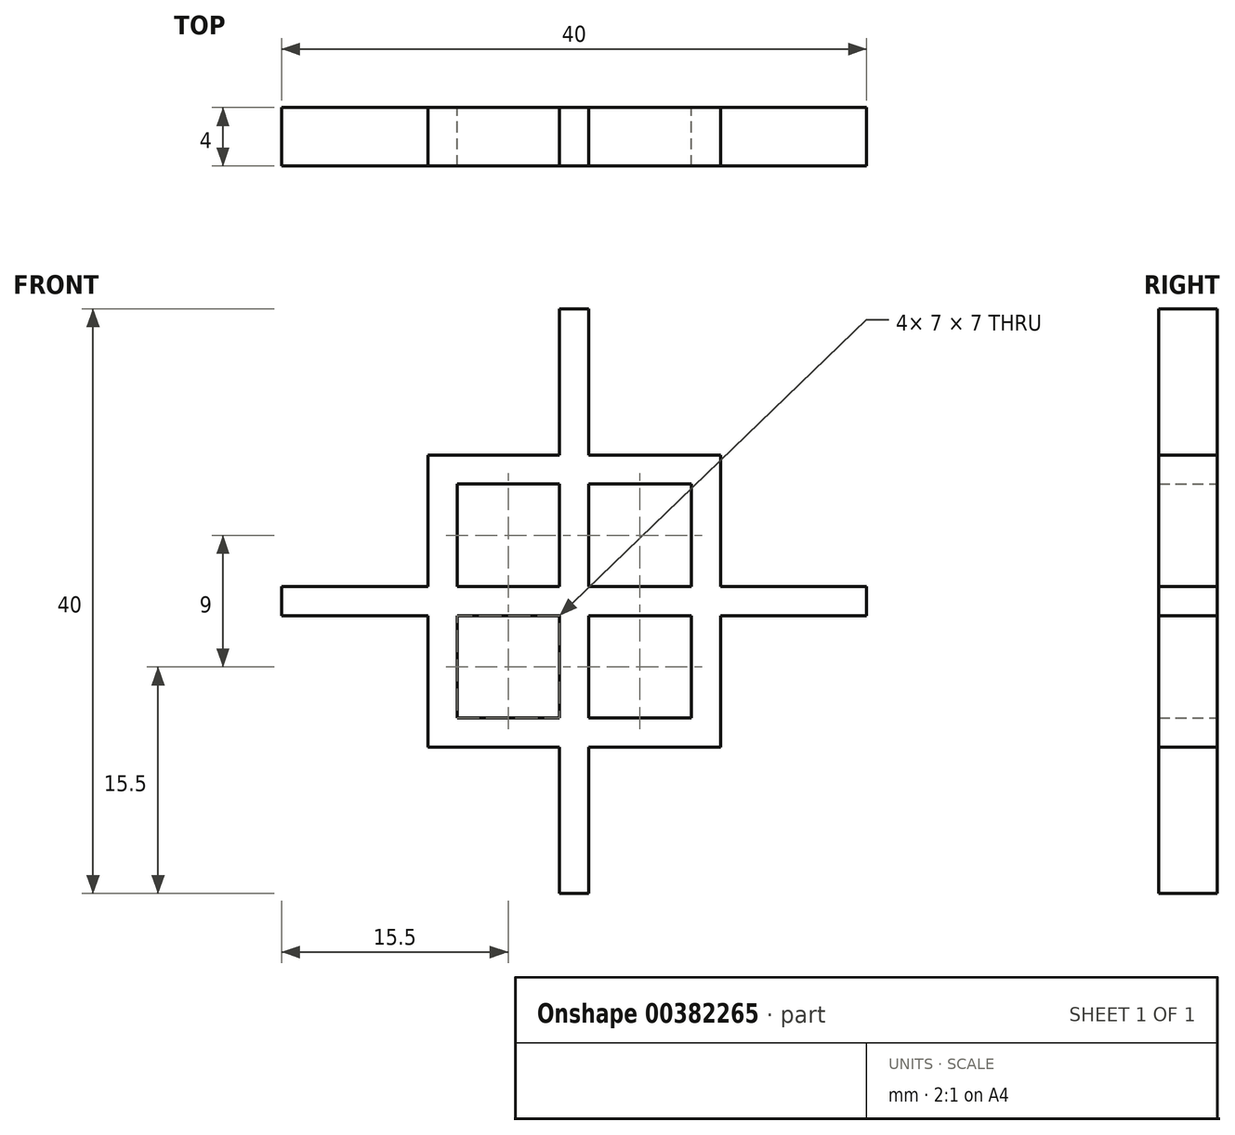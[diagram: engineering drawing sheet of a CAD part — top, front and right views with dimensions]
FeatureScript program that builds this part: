
annotation { "Feature Type Name" : "Feature", "Feature Type Description" : "" }
export const myFeature = defineFeature(function(context is Context, id is Id, definition is map)
    precondition{}
    {
        {
            var Q0;
            Q0=qCreatedBy(makeId("Front.planeOp"),FACE);
            var sketch = newSketch(context, id + "F0", { "sketchPlane" : qUnion([Q0])});
            skPoint(sketch, "E0", {"position": v(20, 0) * mm});
            skPoint(sketch, "E1", {"position": v(0, 20) * mm});
            skLineSegment(sketch, "E2", {"start": v(20, 0) * mm, "end": v(20, 20) * mm});
            skLineSegment(sketch, "E3", {"start": v(20, 20) * mm, "end": v(0, 20) * mm});
            skLineSegment(sketch, "E4", {"start": v(20, 0) * mm, "end": v(20, -20) * mm});
            skLineSegment(sketch, "E5", {"start": v(20, -20) * mm, "end": v(0, -20) * mm});
            skLineSegment(sketch, "E6", {"start": v(0, -20) * mm, "end": v(0, 20) * mm});
            skLineSegment(sketch, "E7.MirrorCS", {"start": v(-20, 20) * mm, "end": v(0, 20) * mm});
            skLineSegment(sketch, "E8.MirrorCS", {"start": v(-20, 0) * mm, "end": v(-20, -20) * mm});
            skLineSegment(sketch, "E9.MirrorCS", {"start": v(-20, -20) * mm, "end": v(0, -20) * mm});
            skLineSegment(sketch, "E10.MirrorCS", {"start": v(-20, 0) * mm, "end": v(-20, 20) * mm});
            skPoint(sketch, "E11", {"position": v(20, -1) * mm});
            skPoint(sketch, "E12", {"position": v(-1, 20) * mm});
            skPoint(sketch, "E13", {"position": v(-20, -1) * mm});
            skPoint(sketch, "E14", {"position": v(1, -20) * mm});
            skPoint(sketch, "E15", {"position": v(8, 19.86) * mm});
            skPoint(sketch, "E16", {"position": v(-8, 20) * mm});
            skPoint(sketch, "E17", {"position": v(20, 8) * mm});
            skPoint(sketch, "E18", {"position": v(20, -8) * mm});
            skLineSegment(sketch, "E19", {"start": v(-20, 0) * mm, "end": v(20, 0) * mm});
            skPoint(sketch, "E20.MirrorP", {"position": v(1, 20) * mm});
            skPoint(sketch, "E21.MirrorP", {"position": v(-20, 8) * mm});
            skPoint(sketch, "E22.MirrorP", {"position": v(-20, -8) * mm});
            skPoint(sketch, "E23.MirrorP", {"position": v(8, -19.86) * mm});
            skPoint(sketch, "E24.MirrorP", {"position": v(-8, -20) * mm});
            skPoint(sketch, "E25.MirrorP", {"position": v(20, 1) * mm});
            skLineSegment(sketch, "E26.bottom", {"start": v(-20, -1) * mm, "end": v(20, -1) * mm});
            skLineSegment(sketch, "E26.top", {"start": v(-20, 1) * mm, "end": v(20, 1) * mm});
            skLineSegment(sketch, "E26.left", {"start": v(-20, -1) * mm, "end": v(-20, 1) * mm});
            skLineSegment(sketch, "E26.right", {"start": v(20, -1) * mm, "end": v(20, 1) * mm});
            skLineSegment(sketch, "E27.bottom", {"start": v(-1, 20) * mm, "end": v(1, 20) * mm});
            skLineSegment(sketch, "E27.top", {"start": v(-1, -20) * mm, "end": v(1, -20) * mm});
            skLineSegment(sketch, "E27.left", {"start": v(-1, 20) * mm, "end": v(-1, -20) * mm});
            skLineSegment(sketch, "E27.right", {"start": v(1, 20) * mm, "end": v(1, -20) * mm});
            skLineSegment(sketch, "E28.bottom", {"start": v(8, 19.86) * mm, "end": v(10, 19.86) * mm});
            skLineSegment(sketch, "E28.top", {"start": v(8, -20) * mm, "end": v(10, -20) * mm});
            skLineSegment(sketch, "E28.left", {"start": v(8, 19.86) * mm, "end": v(8, -20) * mm});
            skLineSegment(sketch, "E28.right", {"start": v(10, 19.86) * mm, "end": v(10, -20) * mm});
            skLineSegment(sketch, "E29.bottom", {"start": v(-8, 20) * mm, "end": v(-10, 20) * mm});
            skLineSegment(sketch, "E29.top", {"start": v(-8, -20) * mm, "end": v(-10, -20) * mm});
            skLineSegment(sketch, "E29.left", {"start": v(-8, 20) * mm, "end": v(-8, -20) * mm});
            skLineSegment(sketch, "E29.right", {"start": v(-10, 20) * mm, "end": v(-10, -20) * mm});
            skLineSegment(sketch, "E30.bottom", {"start": v(-20, 8) * mm, "end": v(20, 8) * mm});
            skLineSegment(sketch, "E30.top", {"start": v(-20, 10) * mm, "end": v(20, 10) * mm});
            skLineSegment(sketch, "E30.left", {"start": v(-20, 8) * mm, "end": v(-20, 10) * mm});
            skLineSegment(sketch, "E30.right", {"start": v(20, 8) * mm, "end": v(20, 10) * mm});
            skLineSegment(sketch, "E31.bottom", {"start": v(-20, -8) * mm, "end": v(20, -8) * mm});
            skLineSegment(sketch, "E31.top", {"start": v(-20, -10) * mm, "end": v(20, -10) * mm});
            skLineSegment(sketch, "E31.left", {"start": v(-20, -8) * mm, "end": v(-20, -10) * mm});
            skLineSegment(sketch, "E31.right", {"start": v(20, -8) * mm, "end": v(20, -10) * mm});
            skSolve(sketch);
        }
        {
            var Q0;
            {var subQ0=sQuery(id+"F0.wireOp",EDGE,"E27.bottom");var subQ1=sQuery(id+"F0.wireOp",EDGE,"E6");var subQ2=makeQuery(id+"F0.imprint","INTERSECT",VERTEX,{"derivedFrom":[subQ1,subQ0]});Q0=makeQuery(id+"F0.imprint","IMPRINT",FACE,{"disambiguationData":[TD([[makeQuery(id+"F0.imprint","IMPRINT",EDGE,{"disambiguationData":[TD([[subQ2,1.0]])],"derivedFrom":subQ1}),1.0]])]});}
            var Q1;
            {var subQ0=sQuery(id+"F0.wireOp",EDGE,"E27.bottom");var subQ1=sQuery(id+"F0.wireOp",EDGE,"E6");var subQ2=makeQuery(id+"F0.imprint","INTERSECT",VERTEX,{"derivedFrom":[subQ1,subQ0]});Q1=makeQuery(id+"F0.imprint","IMPRINT",FACE,{"disambiguationData":[TD([[makeQuery(id+"F0.imprint","IMPRINT",EDGE,{"disambiguationData":[TD([[subQ2,1.0]])],"derivedFrom":subQ1}),-1.0]])]});}
            var Q2;
            {var subQ0=sQuery(id+"F0.wireOp",EDGE,"E30.bottom");var subQ1=sQuery(id+"F0.wireOp",EDGE,"E6");var subQ2=makeQuery(id+"F0.imprint","INTERSECT",VERTEX,{"derivedFrom":[subQ1,subQ0]});Q2=makeQuery(id+"F0.imprint","IMPRINT",FACE,{"disambiguationData":[TD([[makeQuery(id+"F0.imprint","IMPRINT",EDGE,{"disambiguationData":[TD([[subQ2,-1.0]])],"derivedFrom":subQ1}),-1.0]])]});}
            var Q3;
            {var subQ0=sQuery(id+"F0.wireOp",EDGE,"E30.bottom");var subQ1=sQuery(id+"F0.wireOp",EDGE,"E6");var subQ2=makeQuery(id+"F0.imprint","INTERSECT",VERTEX,{"derivedFrom":[subQ1,subQ0]});Q3=makeQuery(id+"F0.imprint","IMPRINT",FACE,{"disambiguationData":[TD([[makeQuery(id+"F0.imprint","IMPRINT",EDGE,{"disambiguationData":[TD([[subQ2,-1.0]])],"derivedFrom":subQ1}),1.0]])]});}
            var Q4;
            {var subQ0=sQuery(id+"F0.wireOp",EDGE,"E30.top");var subQ1=sQuery(id+"F0.wireOp",EDGE,"E27.right");var subQ2=makeQuery(id+"F0.imprint","INTERSECT",VERTEX,{"derivedFrom":[subQ1,subQ0]});Q4=makeQuery(id+"F0.imprint","IMPRINT",FACE,{"disambiguationData":[TD([[makeQuery(id+"F0.imprint","IMPRINT",EDGE,{"disambiguationData":[TD([[subQ2,-1.0]])],"derivedFrom":subQ1}),1.0]])]});}
            var Q5;
            {var subQ0=sQuery(id+"F0.wireOp",EDGE,"E30.top");var subQ1=sQuery(id+"F0.wireOp",EDGE,"E27.left");var subQ2=makeQuery(id+"F0.imprint","INTERSECT",VERTEX,{"derivedFrom":[subQ1,subQ0]});Q5=makeQuery(id+"F0.imprint","IMPRINT",FACE,{"disambiguationData":[TD([[makeQuery(id+"F0.imprint","IMPRINT",EDGE,{"disambiguationData":[TD([[subQ2,-1.0]])],"derivedFrom":subQ1}),-1.0]])]});}
            var Q6;
            {var subQ0=sQuery(id+"F0.wireOp",EDGE,"E30.top");var subQ1=sQuery(id+"F0.wireOp",EDGE,"E28.left");var subQ2=makeQuery(id+"F0.imprint","INTERSECT",VERTEX,{"derivedFrom":[subQ1,subQ0]});Q6=makeQuery(id+"F0.imprint","IMPRINT",FACE,{"disambiguationData":[TD([[makeQuery(id+"F0.imprint","IMPRINT",EDGE,{"disambiguationData":[TD([[subQ2,-1.0]])],"derivedFrom":subQ1}),1.0]])]});}
            var Q7;
            {var subQ0=sQuery(id+"F0.wireOp",EDGE,"E28.left");var subQ1=sQuery(id+"F0.wireOp",EDGE,"E26.top");var subQ2=makeQuery(id+"F0.imprint","INTERSECT",VERTEX,{"derivedFrom":[subQ1,subQ0]});Q7=makeQuery(id+"F0.imprint","IMPRINT",FACE,{"disambiguationData":[TD([[makeQuery(id+"F0.imprint","IMPRINT",EDGE,{"disambiguationData":[TD([[subQ2,-1.0]])],"derivedFrom":subQ1}),1.0]])]});}
            var Q8;
            {var subQ0=sQuery(id+"F0.wireOp",EDGE,"E28.left");var subQ1=sQuery(id+"F0.wireOp",EDGE,"E26.bottom");var subQ2=makeQuery(id+"F0.imprint","INTERSECT",VERTEX,{"derivedFrom":[subQ1,subQ0]});Q8=makeQuery(id+"F0.imprint","IMPRINT",FACE,{"disambiguationData":[TD([[makeQuery(id+"F0.imprint","IMPRINT",EDGE,{"disambiguationData":[TD([[subQ2,-1.0]])],"derivedFrom":subQ1}),-1.0]])]});}
            var Q9;
            {var subQ0=sQuery(id+"F0.wireOp",EDGE,"E26.right");var subQ1=sQuery(id+"F0.wireOp",EDGE,"E19");var subQ2=makeQuery(id+"F0.imprint","INTERSECT",VERTEX,{"derivedFrom":[subQ1,subQ0]});Q9=makeQuery(id+"F0.imprint","IMPRINT",FACE,{"disambiguationData":[TD([[makeQuery(id+"F0.imprint","IMPRINT",EDGE,{"disambiguationData":[TD([[subQ2,1.0]])],"derivedFrom":subQ1}),1.0]])]});}
            var Q10;
            {var subQ0=sQuery(id+"F0.wireOp",EDGE,"E26.right");var subQ1=sQuery(id+"F0.wireOp",EDGE,"E19");var subQ2=makeQuery(id+"F0.imprint","INTERSECT",VERTEX,{"derivedFrom":[subQ1,subQ0]});Q10=makeQuery(id+"F0.imprint","IMPRINT",FACE,{"disambiguationData":[TD([[makeQuery(id+"F0.imprint","IMPRINT",EDGE,{"disambiguationData":[TD([[subQ2,1.0]])],"derivedFrom":subQ1}),-1.0]])]});}
            var Q11;
            {var subQ0=sQuery(id+"F0.wireOp",EDGE,"E28.left");var subQ1=sQuery(id+"F0.wireOp",EDGE,"E19");var subQ2=makeQuery(id+"F0.imprint","INTERSECT",VERTEX,{"derivedFrom":[subQ1,subQ0]});Q11=makeQuery(id+"F0.imprint","IMPRINT",FACE,{"disambiguationData":[TD([[makeQuery(id+"F0.imprint","IMPRINT",EDGE,{"disambiguationData":[TD([[subQ2,-1.0]])],"derivedFrom":subQ1}),-1.0]])]});}
            var Q12;
            {var subQ0=sQuery(id+"F0.wireOp",EDGE,"E28.left");var subQ1=sQuery(id+"F0.wireOp",EDGE,"E19");var subQ2=makeQuery(id+"F0.imprint","INTERSECT",VERTEX,{"derivedFrom":[subQ1,subQ0]});Q12=makeQuery(id+"F0.imprint","IMPRINT",FACE,{"disambiguationData":[TD([[makeQuery(id+"F0.imprint","IMPRINT",EDGE,{"disambiguationData":[TD([[subQ2,-1.0]])],"derivedFrom":subQ1}),1.0]])]});}
            var Q13;
            {var subQ0=sQuery(id+"F0.wireOp",EDGE,"E31.bottom");var subQ1=sQuery(id+"F0.wireOp",EDGE,"E28.left");var subQ2=makeQuery(id+"F0.imprint","INTERSECT",VERTEX,{"derivedFrom":[subQ1,subQ0]});Q13=makeQuery(id+"F0.imprint","IMPRINT",FACE,{"disambiguationData":[TD([[makeQuery(id+"F0.imprint","IMPRINT",EDGE,{"disambiguationData":[TD([[subQ2,-1.0]])],"derivedFrom":subQ1}),1.0]])]});}
            var Q14;
            {var subQ0=sQuery(id+"F0.wireOp",EDGE,"E31.bottom");var subQ1=sQuery(id+"F0.wireOp",EDGE,"E27.right");var subQ2=makeQuery(id+"F0.imprint","INTERSECT",VERTEX,{"derivedFrom":[subQ1,subQ0]});Q14=makeQuery(id+"F0.imprint","IMPRINT",FACE,{"disambiguationData":[TD([[makeQuery(id+"F0.imprint","IMPRINT",EDGE,{"disambiguationData":[TD([[subQ2,-1.0]])],"derivedFrom":subQ1}),1.0]])]});}
            var Q15;
            {var subQ0=sQuery(id+"F0.wireOp",EDGE,"E31.top");var subQ1=sQuery(id+"F0.wireOp",EDGE,"E6");var subQ2=makeQuery(id+"F0.imprint","INTERSECT",VERTEX,{"derivedFrom":[subQ1,subQ0]});Q15=makeQuery(id+"F0.imprint","IMPRINT",FACE,{"disambiguationData":[TD([[makeQuery(id+"F0.imprint","IMPRINT",EDGE,{"disambiguationData":[TD([[subQ2,-1.0]])],"derivedFrom":subQ1}),-1.0]])]});}
            var Q16;
            {var subQ0=sQuery(id+"F0.wireOp",EDGE,"E31.top");var subQ1=sQuery(id+"F0.wireOp",EDGE,"E6");var subQ2=makeQuery(id+"F0.imprint","INTERSECT",VERTEX,{"derivedFrom":[subQ1,subQ0]});Q16=makeQuery(id+"F0.imprint","IMPRINT",FACE,{"disambiguationData":[TD([[makeQuery(id+"F0.imprint","IMPRINT",EDGE,{"disambiguationData":[TD([[subQ2,-1.0]])],"derivedFrom":subQ1}),1.0]])]});}
            var Q17;
            {var subQ0=sQuery(id+"F0.wireOp",EDGE,"E27.top");var subQ1=sQuery(id+"F0.wireOp",EDGE,"E6");var subQ2=makeQuery(id+"F0.imprint","INTERSECT",VERTEX,{"derivedFrom":[subQ1,subQ0]});Q17=makeQuery(id+"F0.imprint","IMPRINT",FACE,{"disambiguationData":[TD([[makeQuery(id+"F0.imprint","IMPRINT",EDGE,{"disambiguationData":[TD([[subQ2,-1.0]])],"derivedFrom":subQ1}),-1.0]])]});}
            var Q18;
            {var subQ0=sQuery(id+"F0.wireOp",EDGE,"E27.top");var subQ1=sQuery(id+"F0.wireOp",EDGE,"E6");var subQ2=makeQuery(id+"F0.imprint","INTERSECT",VERTEX,{"derivedFrom":[subQ1,subQ0]});Q18=makeQuery(id+"F0.imprint","IMPRINT",FACE,{"disambiguationData":[TD([[makeQuery(id+"F0.imprint","IMPRINT",EDGE,{"disambiguationData":[TD([[subQ2,-1.0]])],"derivedFrom":subQ1}),1.0]])]});}
            var Q19;
            {var subQ0=sQuery(id+"F0.wireOp",EDGE,"E31.bottom");var subQ1=sQuery(id+"F0.wireOp",EDGE,"E27.left");var subQ2=makeQuery(id+"F0.imprint","INTERSECT",VERTEX,{"derivedFrom":[subQ1,subQ0]});Q19=makeQuery(id+"F0.imprint","IMPRINT",FACE,{"disambiguationData":[TD([[makeQuery(id+"F0.imprint","IMPRINT",EDGE,{"disambiguationData":[TD([[subQ2,-1.0]])],"derivedFrom":subQ1}),-1.0]])]});}
            var Q20;
            {var subQ0=sQuery(id+"F0.wireOp",EDGE,"E31.bottom");var subQ1=sQuery(id+"F0.wireOp",EDGE,"E29.left");var subQ2=makeQuery(id+"F0.imprint","INTERSECT",VERTEX,{"derivedFrom":[subQ1,subQ0]});Q20=makeQuery(id+"F0.imprint","IMPRINT",FACE,{"disambiguationData":[TD([[makeQuery(id+"F0.imprint","IMPRINT",EDGE,{"disambiguationData":[TD([[subQ2,-1.0]])],"derivedFrom":subQ1}),-1.0]])]});}
            var Q21;
            {var subQ0=sQuery(id+"F0.wireOp",EDGE,"E29.right");var subQ1=sQuery(id+"F0.wireOp",EDGE,"E26.bottom");var subQ2=makeQuery(id+"F0.imprint","INTERSECT",VERTEX,{"derivedFrom":[subQ1,subQ0]});Q21=makeQuery(id+"F0.imprint","IMPRINT",FACE,{"disambiguationData":[TD([[makeQuery(id+"F0.imprint","IMPRINT",EDGE,{"disambiguationData":[TD([[subQ2,-1.0]])],"derivedFrom":subQ1}),-1.0]])]});}
            var Q22;
            {var subQ0=sQuery(id+"F0.wireOp",EDGE,"E29.right");var subQ1=sQuery(id+"F0.wireOp",EDGE,"E26.top");var subQ2=makeQuery(id+"F0.imprint","INTERSECT",VERTEX,{"derivedFrom":[subQ1,subQ0]});Q22=makeQuery(id+"F0.imprint","IMPRINT",FACE,{"disambiguationData":[TD([[makeQuery(id+"F0.imprint","IMPRINT",EDGE,{"disambiguationData":[TD([[subQ2,-1.0]])],"derivedFrom":subQ1}),1.0]])]});}
            var Q23;
            {var subQ0=sQuery(id+"F0.wireOp",EDGE,"E30.top");var subQ1=sQuery(id+"F0.wireOp",EDGE,"E29.left");var subQ2=makeQuery(id+"F0.imprint","INTERSECT",VERTEX,{"derivedFrom":[subQ1,subQ0]});Q23=makeQuery(id+"F0.imprint","IMPRINT",FACE,{"disambiguationData":[TD([[makeQuery(id+"F0.imprint","IMPRINT",EDGE,{"disambiguationData":[TD([[subQ2,-1.0]])],"derivedFrom":subQ1}),-1.0]])]});}
            var Q24;
            {var subQ0=sQuery(id+"F0.wireOp",EDGE,"E29.right");var subQ1=sQuery(id+"F0.wireOp",EDGE,"E19");var subQ2=makeQuery(id+"F0.imprint","INTERSECT",VERTEX,{"derivedFrom":[subQ1,subQ0]});Q24=makeQuery(id+"F0.imprint","IMPRINT",FACE,{"disambiguationData":[TD([[makeQuery(id+"F0.imprint","IMPRINT",EDGE,{"disambiguationData":[TD([[subQ2,-1.0]])],"derivedFrom":subQ1}),1.0]])]});}
            var Q25;
            {var subQ0=sQuery(id+"F0.wireOp",EDGE,"E29.right");var subQ1=sQuery(id+"F0.wireOp",EDGE,"E19");var subQ2=makeQuery(id+"F0.imprint","INTERSECT",VERTEX,{"derivedFrom":[subQ1,subQ0]});Q25=makeQuery(id+"F0.imprint","IMPRINT",FACE,{"disambiguationData":[TD([[makeQuery(id+"F0.imprint","IMPRINT",EDGE,{"disambiguationData":[TD([[subQ2,-1.0]])],"derivedFrom":subQ1}),-1.0]])]});}
            var Q26;
            {var subQ0=sQuery(id+"F0.wireOp",EDGE,"E26.left");var subQ1=sQuery(id+"F0.wireOp",EDGE,"E19");var subQ2=makeQuery(id+"F0.imprint","INTERSECT",VERTEX,{"derivedFrom":[subQ1,subQ0]});Q26=makeQuery(id+"F0.imprint","IMPRINT",FACE,{"disambiguationData":[TD([[makeQuery(id+"F0.imprint","IMPRINT",EDGE,{"disambiguationData":[TD([[subQ2,-1.0]])],"derivedFrom":subQ1}),1.0]])]});}
            var Q27;
            {var subQ0=sQuery(id+"F0.wireOp",EDGE,"E26.left");var subQ1=sQuery(id+"F0.wireOp",EDGE,"E19");var subQ2=makeQuery(id+"F0.imprint","INTERSECT",VERTEX,{"derivedFrom":[subQ1,subQ0]});Q27=makeQuery(id+"F0.imprint","IMPRINT",FACE,{"disambiguationData":[TD([[makeQuery(id+"F0.imprint","IMPRINT",EDGE,{"disambiguationData":[TD([[subQ2,-1.0]])],"derivedFrom":subQ1}),-1.0]])]});}
            extrude(context, id + "F1", {"entities" : qUnion([Q0, Q1, Q2, Q3, Q4, Q5, Q6, Q7, Q8, Q9, Q10, Q11, Q12, Q13, Q14, Q15, Q16, Q17, Q18, Q19, Q20, Q21, Q22, Q23, Q24, Q25, Q26, Q27]), "depth" : 4 * mm});
        }
    });
